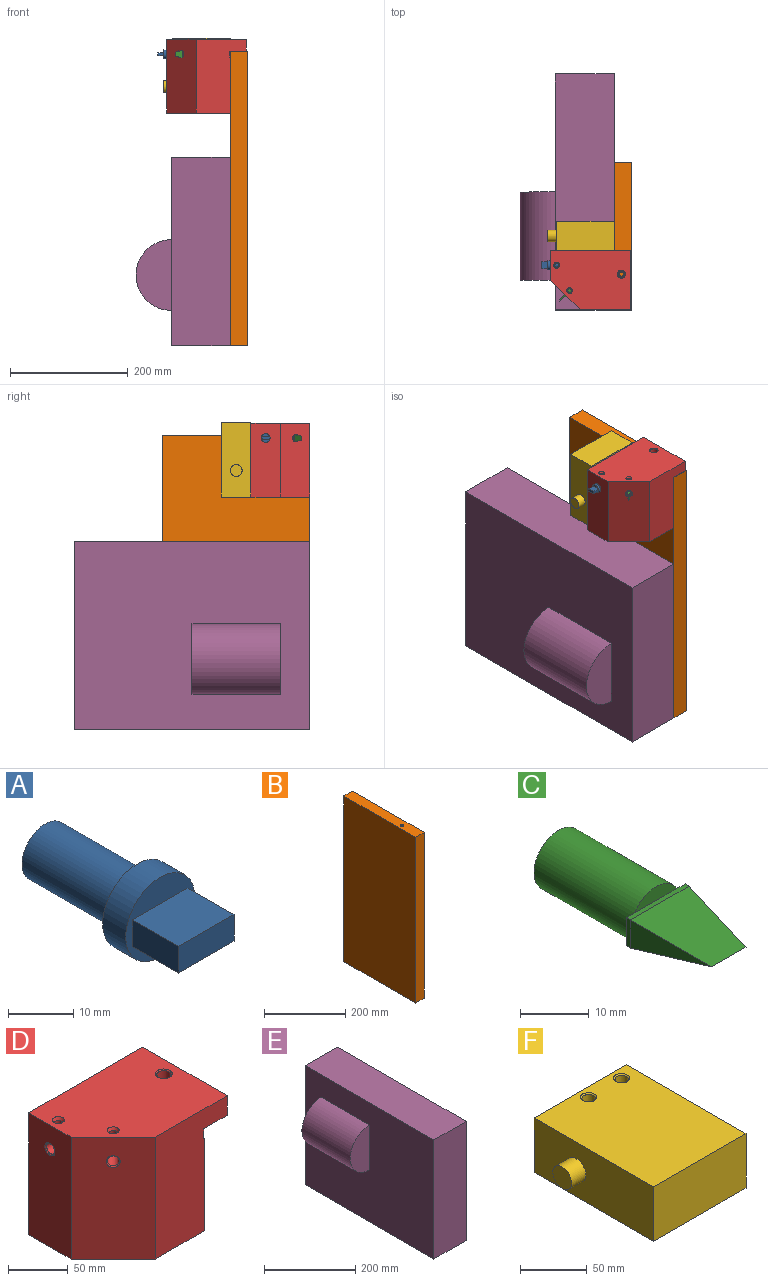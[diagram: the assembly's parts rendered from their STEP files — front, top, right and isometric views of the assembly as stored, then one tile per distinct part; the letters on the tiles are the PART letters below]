
ASSEMBLY  parts=6 mates=5
PART A: 10 faces, bbox 15x35x15 mm
  f0: plane 15x15mm, normal (0,-1,0), area 116.7mm2, adj f3,f5,f6,f7,f8
  f1: cylinder r=5mm len=20mm, axis (0,1,0), area 628.3mm2, adj f2,f4
  f2: plane 10x10mm, normal (0,1,0), area 78.5mm2, adj f1
  f3: cylinder r=7.5mm len=15mm, axis (0,1,0), area 235.6mm2, adj f0,f4
  f4: plane 15x15mm, normal (0,1,0), area 98.2mm2, adj f1,f3
  f5: plane 12x10mm, normal (0,0,1), area 120mm2, adj f0,f6,f8,f9
  f6: plane 10x5mm, normal (-1,0,0), area 50mm2, adj f0,f5,f7,f9
  f7: plane 12x10mm, normal (0,0,-1), area 120mm2, adj f0,f6,f8,f9
  f8: plane 10x5mm, normal (1,0,0), area 50mm2, adj f0,f5,f7,f9
  f9: plane 12x5mm, normal (0,-1,0), area 60mm2, adj f5,f6,f7,f8
PART B: 9 faces, bbox 30x250x500 mm
  f0: plane 250x30mm, normal (0,0,-1), area 7500mm2, adj f1,f3,f4,f5
  f1: plane 500x30mm, normal (0,1,0), area 15000mm2, adj f0,f2,f4,f5
  f2: plane 250x30mm, normal (0,0,1), area 7439.2mm2, adj f1,f3,f4,f5,f8
  f3: plane 500x30mm, normal (0,-1,0), area 15000mm2, adj f0,f2,f4,f5
  f4: plane 500x250mm, normal (-1,0,0), area 125000mm2, adj f0,f1,f2,f3
  f5: plane 500x250mm, normal (1,0,0), area 125000mm2, adj f0,f1,f2,f3
  f6: cylinder r=3.4mm len=24mm, axis (0,0,1), area 512.7mm2, adj f7,f8
  f7: plane 6.8x6.8mm, normal (0,0,1), area 36.3mm2, adj f6
  f8: cone r=3.4mm half-angle=45deg, axis (0,0,1), area 34.7mm2, adj f2,f6
PART C: 14 faces, bbox 12x35x10 mm
  f0: plane 8.66x2.5mm, normal (0,-1,0), area 15.4mm2, adj f1,f9
  f1: cylinder r=5mm len=20mm, axis (0,1,0), area 628.3mm2, adj f0,f2,f3,f4,f5
  f2: plane 8.66x2.5mm, normal (0,-1,0), area 15.4mm2, adj f1,f7
  f3: plane 10x10mm, normal (0,1,0), area 78.5mm2, adj f1
  f4: plane 5x1.67mm, normal (0,1,0), area 6.1mm2, adj f1,f7,f8,f9
  f5: plane 5x1.67mm, normal (0,1,0), area 6.1mm2, adj f1,f6,f7,f9
  f6: plane 5x0.82mm, normal (-1,0,0), area 4.1mm2, adj f5,f7,f9,f10
  f7: plane 12x0.82mm, normal (0,0,-1), area 9.9mm2, adj f2,f4,f5,f6,f8,f11
  f8: plane 5x0.82mm, normal (1,0,0), area 4.1mm2, adj f4,f7,f9,f13
  f9: plane 12x0.82mm, normal (0,0,1), area 9.9mm2, adj f0,f4,f5,f6,f8,f12
  f10: plane 14.18x5mm, normal (-0.98,-0.17,0), area 36mm2, adj f6,f11,f12
  f11: plane 14.18x12mm, normal (0,-0.17,-0.98), area 136.8mm2, adj f7,f10,f12,f13
  f12: plane 14.18x12mm, normal (0,-0.17,0.98), area 136.8mm2, adj f9,f10,f11,f13
  f13: plane 14.18x5mm, normal (0.98,-0.17,0), area 36mm2, adj f8,f11,f12
PART D: 29 faces, bbox 135x100x125 mm
  f0: cylinder r=5mm len=24.04mm, axis (-0.71,-0.71,0), area 715.1mm2, adj f11,f23,f27
  f1: cylinder r=5mm len=24mm, axis (-1,0,0), area 715.1mm2, adj f12,f24,f25
  f2: plane 125x85mm, normal (0,-1,0), area 7780mm2, adj f3,f5,f6,f7,f8,f10,f14,f15
  f3: plane 135x100mm, normal (0,0,1), area 11939mm2, adj f2,f4,f8,f9,f10,f22,f26,f28
  f4: plane 125x50mm, normal (-1,0,0), area 6136.9mm2, adj f3,f5,f9,f10,f24
  f5: plane 108x100mm, normal (0,0,-1), area 9550mm2, adj f2,f4,f6,f9,f10
  f6: plane 100x95mm, normal (1,0,0), area 9500mm2, adj f2,f5,f9,f14
  f7: plane 100x28mm, normal (0,0,-1), area 2686.9mm2, adj f2,f8,f9,f13,f15
  f8: plane 100x20mm, normal (1,0,0), area 2000mm2, adj f2,f3,f7,f9
  f9: plane 135x125mm, normal (0,1,0), area 13872.9mm2, adj f3,f4,f5,f6,f7,f8,f14,f15
  f10: plane 125x50mm, normal (-0.71,-0.71,0), area 8725.7mm2, adj f2,f3,f4,f5,f23
  f11: plane 10x7.07mm, normal (-0.71,-0.71,0), area 78.5mm2, adj f0
  f12: plane 10x10mm, normal (-1,0,0), area 78.5mm2, adj f1
  f13: cylinder r=6mm len=19mm, axis (0,0,1), area 716.3mm2, adj f7,f22
  f14: plane 100x1mm, normal (0,0,1), area 100mm2, adj f2,f6,f9,f15
  f15: plane 100x10mm, normal (1,0,0), area 1000mm2, adj f2,f7,f9,f14
  f16: cylinder r=3.4mm len=17.23mm, axis (0,1,0), area 368.1mm2, adj f17,f18
  f17: cone r=3.4mm half-angle=30deg, axis (0,1,0), area 84.4mm2, adj f9,f16
  f18: cone r=0mm half-angle=59deg, axis (0,1,0), area 42.4mm2, adj f16
  f19: cylinder r=3.4mm len=17.23mm, axis (0,1,0), area 368.1mm2, adj f20,f21
  f20: cone r=3.4mm half-angle=30deg, axis (0,1,0), area 84.4mm2, adj f9,f19
  f21: cone r=0mm half-angle=59deg, axis (0,1,0), area 42.4mm2, adj f19
  f22: cone r=6mm half-angle=45deg, axis (0,0,1), area 57.8mm2, adj f3,f13
  f23: cone r=5mm half-angle=45deg, axis (-0.71,-0.71,0), area 48.9mm2, adj f0,f10
  f24: cone r=5mm half-angle=45deg, axis (-1,0,0), area 48.9mm2, adj f1,f4
  f25: cylinder r=3.4mm len=18.56mm, axis (0,0,1), area 381.8mm2, adj f1,f26
  f26: cone r=3.4mm half-angle=30deg, axis (0,0,1), area 84.4mm2, adj f3,f25
  f27: cylinder r=3.4mm len=18.56mm, axis (0,0,1), area 381.8mm2, adj f0,f28
  f28: cone r=3.4mm half-angle=30deg, axis (0,0,1), area 84.4mm2, adj f3,f27
PART E: 9 faces, bbox 160x400x320 mm
  f0: plane 400x320mm, normal (-1,0,0), area 110000mm2, adj f1,f2,f3,f4,f6,f7,f8
  f1: plane 400x100mm, normal (0,0,-1), area 40000mm2, adj f0,f2,f4,f5
  f2: plane 320x100mm, normal (0,1,0), area 32000mm2, adj f0,f1,f3,f5
  f3: plane 400x100mm, normal (0,0,1), area 40000mm2, adj f0,f2,f4,f5
  f4: plane 320x100mm, normal (0,-1,0), area 32000mm2, adj f0,f1,f3,f5
  f5: plane 400x320mm, normal (1,0,0), area 128000mm2, adj f1,f2,f3,f4
  f6: cylinder r=60mm len=150mm, axis (0,1,0), area 28274.3mm2, adj f0,f7,f8
  f7: plane 120x60mm, normal (0,-1,0), area 5654.9mm2, adj f0,f6
  f8: plane 120x60mm, normal (0,1,0), area 5654.9mm2, adj f0,f6
PART F: 14 faces, bbox 113x127x50 mm
  f0: plane 127x98mm, normal (0,0,1), area 12219.8mm2, adj f1,f3,f4,f5,f12,f13
  f1: plane 98x50mm, normal (0,-1,0), area 4900mm2, adj f0,f2,f4,f5
  f2: plane 127x98mm, normal (0,0,-1), area 12219.8mm2, adj f1,f3,f4,f5,f10,f11
  f3: plane 98x50mm, normal (0,1,0), area 4900mm2, adj f0,f2,f4,f5
  f4: plane 127x50mm, normal (-1,0,0), area 6035.8mm2, adj f0,f1,f2,f3,f6
  f5: plane 127x50mm, normal (1,0,0), area 6350mm2, adj f0,f1,f2,f3
  f6: cylinder r=10mm len=20mm, axis (1,0,0), area 942.5mm2, adj f4,f7
  f7: plane 20x20mm, normal (-1,0,0), area 314.2mm2, adj f6
  f8: cylinder r=5mm len=48mm, axis (0,0,1), area 1508mm2, adj f10,f13
  f9: cylinder r=5mm len=48mm, axis (0,0,1), area 1508mm2, adj f11,f12
  f10: cone r=5mm half-angle=45deg, axis (0,0,-1), area 48.9mm2, adj f2,f8
  f11: cone r=5mm half-angle=45deg, axis (0,0,-1), area 48.9mm2, adj f2,f9
  f12: cone r=5mm half-angle=45deg, axis (0,0,1), area 48.9mm2, adj f0,f9
  f13: cone r=5mm half-angle=45deg, axis (0,0,1), area 48.9mm2, adj f0,f8
PLACE A rot(axis=(0,0,-1),90deg) t=(100.62,-78.23,-166.62)mm
PLACE B t=(218.62,38.76,-542.82)mm
PLACE C rot(axis=(-0.36,-0.86,-0.36),98.4deg) t=(119.76,-114.09,-166.62)mm
PLACE D t=(368.27,-53.23,-104.86)mm
PLACE E rot(axis=(1,0,0),180deg) t=(188.62,-79.77,-357.07)mm
PLACE F rot(axis=(-1,0,0),90deg) t=(188.62,-3.23,-139.62)mm
MATE fastened A.f1 <-> D.f1  axis (1,0,0) through (80.62,-78.23,-166.62)mm
MATE fastened C.f1 <-> D.f23  axis (-0.71,-0.71,0) through (105.62,-128.23,-166.62)mm
MATE fastened D.f22 <-> B.f6  axis (0,0,-1) through (200.62,-93.23,-161.62)mm
MATE fastened E.f5 <-> B.f4  axis (1,0,0) through (188.62,-153.23,-661.62)mm
MATE fastened D.f16 <-> F.f11  axis (0,1,0) through (173.62,-53.23,-256.62)mm
